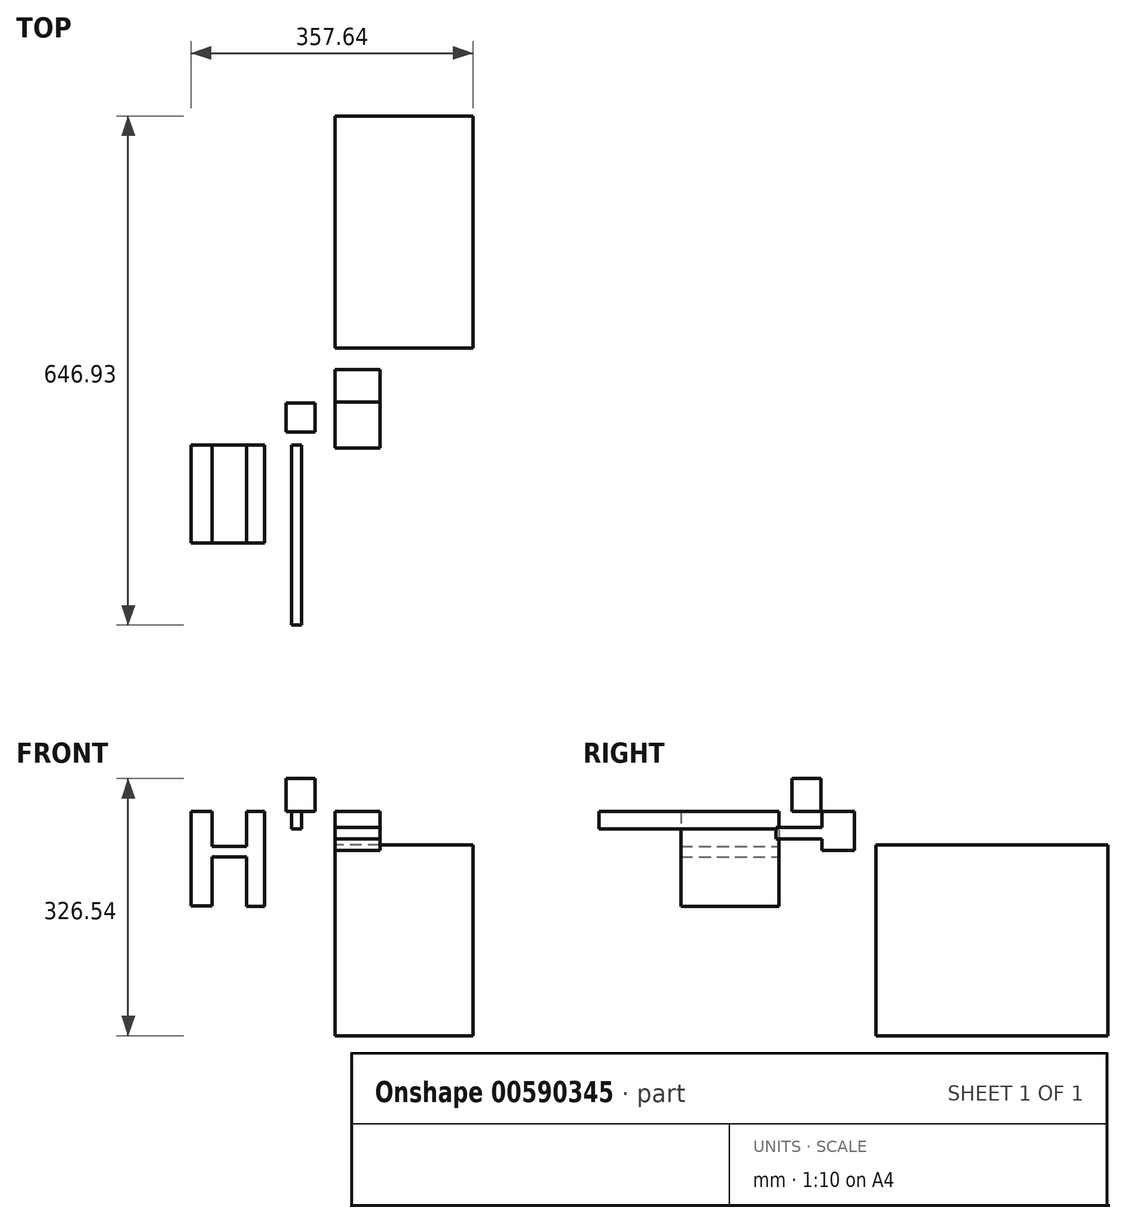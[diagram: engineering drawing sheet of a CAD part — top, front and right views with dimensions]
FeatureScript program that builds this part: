
annotation { "Feature Type Name" : "Feature", "Feature Type Description" : "" }
export const myFeature = defineFeature(function(context is Context, id is Id, definition is map)
    precondition{}
    {
        {
            var Q0;
            Q0=qCreatedBy(makeId("Top.planeOp"),FACE);
            var sketch = newSketch(context, id + "F0", { "sketchPlane" : qUnion([Q0])});
            skLineSegment(sketch, "E0.bottom", {"start": v(-61.98, 53.7) * mm, "end": v(-25.24, 53.7) * mm});
            skLineSegment(sketch, "E0.top", {"start": v(-61.98, 16.97) * mm, "end": v(-25.24, 16.97) * mm});
            skLineSegment(sketch, "E0.left", {"start": v(-61.98, 53.7) * mm, "end": v(-61.98, 16.97) * mm});
            skLineSegment(sketch, "E0.right", {"start": v(-25.24, 53.7) * mm, "end": v(-25.24, 16.97) * mm});
            skSolve(sketch);
        }
        {
            var Q0;
            Q0 = qSketchRegion(id + "F0", true);
            extrude(context, id + "F1", {"entities" : qUnion([Q0]), "depth" : 41.9 * mm, "offsetDistance" : 25.4 * mm});
        }
        {
            var Q0;
            Q0=qCreatedBy(makeId("Right.planeOp"),FACE);
            var sketch = newSketch(context, id + "F2", { "sketchPlane" : qUnion([Q0])});
            skLineSegment(sketch, "E1.bottom", {"start": v(-3.45, -2.4) * mm, "end": v(45.33, -2.4) * mm});
            skLineSegment(sketch, "E1.top", {"start": v(-3.45, -60.14) * mm, "end": v(45.33, -60.14) * mm});
            skLineSegment(sketch, "E1.left", {"start": v(-3.45, -2.4) * mm, "end": v(-3.45, -60.14) * mm});
            skLineSegment(sketch, "E1.right", {"start": v(45.33, -2.4) * mm, "end": v(45.33, -60.14) * mm});
            skSolve(sketch);
        }
        {
            var Q0;
            Q0=makeQuery(id+"F2.imprint","IMPRINT",FACE,{"disambiguationData":[TD([[makeQuery(id+"F2.imprint","IMPRINT",EDGE,{"derivedFrom":sQuery(id+"F2.wireOp",EDGE,"E1.bottom")}),-1.0]])]});
            var sketch = newSketch(context, id + "F3", { "sketchPlane" : qUnion([Q0])});
            skLineSegment(sketch, "E2.bottom", {"start": v(55.1, 0) * mm, "end": v(96.37, 0) * mm});
            skLineSegment(sketch, "E2.top", {"start": v(55.1, -49.58) * mm, "end": v(96.37, -49.58) * mm});
            skLineSegment(sketch, "E2.left", {"start": v(55.1, 0) * mm, "end": v(55.1, -49.58) * mm});
            skLineSegment(sketch, "E2.right", {"start": v(96.37, 0) * mm, "end": v(96.37, -49.58) * mm});
            skLineSegment(sketch, "E3.bottom", {"start": v(73.86, -20.04) * mm, "end": v(-71.23, -20.04) * mm});
            skLineSegment(sketch, "E3.top", {"start": v(73.86, -34.81) * mm, "end": v(-71.23, -34.81) * mm});
            skLineSegment(sketch, "E3.left", {"start": v(73.86, -20.04) * mm, "end": v(73.86, -34.81) * mm});
            skLineSegment(sketch, "E3.right", {"start": v(-71.23, -20.04) * mm, "end": v(-71.23, -34.81) * mm});
            skSolve(sketch);
        }
        {
            var Q0;
            {var subQ4=sQuery(id+"F3.wireOp",EDGE,"E2.bottom");Q0=makeQuery(id+"F3.imprint","IMPRINT",FACE,{"disambiguationData":[TD([[makeQuery(id+"F3.imprint","IMPRINT",EDGE,{"derivedFrom":subQ4}),-1.0]])]});}
            var Q1;
            {var subQ5=sQuery(id+"F3.wireOp",EDGE,"E3.left");Q1=makeQuery(id+"F3.imprint","IMPRINT",FACE,{"disambiguationData":[TD([[makeQuery(id+"F3.imprint","IMPRINT",EDGE,{"derivedFrom":subQ5}),-1.0]])]});}
            var Q2;
            {var subQ0=sQuery(id+"F3.wireOp",EDGE,"E3.bottom");var subQ1=sQuery(id+"F3.wireOp",EDGE,"E2.left");var subQ2=makeQuery(id+"F3.imprint","INTERSECT",VERTEX,{"derivedFrom":[subQ1,subQ0]});Q2=makeQuery(id+"F3.imprint","IMPRINT",FACE,{"disambiguationData":[TD([[makeQuery(id+"F3.imprint","IMPRINT",EDGE,{"disambiguationData":[TD([[subQ2,-1.0]])],"derivedFrom":subQ1}),-1.0]])]});}
            var Q3;
            {var subQ0=sQuery(id+"F3.wireOp",EDGE,"E3.bottom");var subQ1=makeQuery(id+"F2.imprint","IMPRINT",EDGE,{"derivedFrom":sQuery(id+"F2.wireOp",EDGE,"E1.right")});var subQ2=makeQuery(id+"F3.imprint","INTERSECT",VERTEX,{"derivedFrom":[subQ1,subQ0]});Q3=makeQuery(id+"F3.imprint","IMPRINT",FACE,{"disambiguationData":[TD([[makeQuery(id+"F3.imprint","IMPRINT",EDGE,{"disambiguationData":[TD([[subQ2,-1.0]])],"derivedFrom":subQ0}),1.0]])]});}
            extrude(context, id + "F4", {"entities" : qUnion([Q0, Q1, Q2, Q3]), "depth" : 57.15 * mm, "offsetDistance" : 25.4 * mm});
        }
        {
            var Q0;
            Q0=qCreatedBy(makeId("Right.planeOp"),FACE);
            var sketch = newSketch(context, id + "F5", { "sketchPlane" : qUnion([Q0])});
            skLineSegment(sketch, "E4.bottom", {"start": v(123.59, -42.1) * mm, "end": v(418.33, -42.1) * mm});
            skLineSegment(sketch, "E4.top", {"start": v(123.59, -284.63) * mm, "end": v(418.33, -284.63) * mm});
            skLineSegment(sketch, "E4.left", {"start": v(123.59, -42.1) * mm, "end": v(123.59, -284.63) * mm});
            skLineSegment(sketch, "E4.right", {"start": v(418.33, -42.1) * mm, "end": v(418.33, -284.63) * mm});
            skSolve(sketch);
        }
        {
            var Q0;
            Q0=makeQuery(id+"F5.imprint","IMPRINT",FACE,{"disambiguationData":[TD([[makeQuery(id+"F5.imprint","IMPRINT",EDGE,{"derivedFrom":sQuery(id+"F5.wireOp",EDGE,"E4.bottom")}),-1.0]])]});
            extrude(context, id + "F6", {"entities" : qUnion([Q0]), "depth" : 175.26 * mm, "offsetDistance" : 25.4 * mm});
        }
        {
            var Q0;
            Q0=qCreatedBy(makeId("Front.planeOp"),FACE);
            var sketch = newSketch(context, id + "F7", { "sketchPlane" : qUnion([Q0])});
            skLineSegment(sketch, "E5.bottom", {"start": v(-156.26, 0) * mm, "end": v(-182.38, 0) * mm});
            skLineSegment(sketch, "E5.top", {"start": v(-156.26, -120.05) * mm, "end": v(-182.38, -120.05) * mm});
            skLineSegment(sketch, "E5.left", {"start": v(-156.26, 0) * mm, "end": v(-156.26, -120.05) * mm});
            skLineSegment(sketch, "E5.right", {"start": v(-182.38, 0) * mm, "end": v(-182.38, -120.05) * mm});
            skLineSegment(sketch, "E6.bottom", {"start": v(-163.44, -44.3) * mm, "end": v(-96.83, -44.3) * mm});
            skLineSegment(sketch, "E6.top", {"start": v(-163.44, -57.36) * mm, "end": v(-96.83, -57.36) * mm});
            skLineSegment(sketch, "E6.left", {"start": v(-163.44, -44.3) * mm, "end": v(-163.44, -57.36) * mm});
            skLineSegment(sketch, "E6.right", {"start": v(-96.83, -44.3) * mm, "end": v(-96.83, -57.36) * mm});
            skLineSegment(sketch, "E7.bottom", {"start": v(-112.5, 0) * mm, "end": v(-89.64, 0) * mm});
            skLineSegment(sketch, "E7.top", {"start": v(-112.5, -120.7) * mm, "end": v(-89.64, -120.7) * mm});
            skLineSegment(sketch, "E7.left", {"start": v(-112.5, 0) * mm, "end": v(-112.5, -120.7) * mm});
            skLineSegment(sketch, "E7.right", {"start": v(-89.64, 0) * mm, "end": v(-89.64, -120.7) * mm});
            skSolve(sketch);
        }
        {
            var Q0;
            Q0 = qSketchRegion(id + "F7", true);
            var Q1;
            {var subQ4=sQuery(id+"F7.wireOp",EDGE,"E5.bottom");Q1=makeQuery(id+"F7.imprint","IMPRINT",FACE,{"disambiguationData":[TD([[makeQuery(id+"F7.imprint","IMPRINT",EDGE,{"derivedFrom":subQ4}),1.0]])]});}
            extrude(context, id + "F8", {"entities" : qUnion([Q0, Q1]), "depth" : 124.46 * mm, "offsetDistance" : 25.4 * mm});
        }
        {
            var Q0;
            Q0=qCreatedBy(makeId("Front.planeOp"),FACE);
            var sketch = newSketch(context, id + "F9", { "sketchPlane" : qUnion([Q0])});
            skLineSegment(sketch, "E8.bottom", {"start": v(-54.83, -48.87) * mm, "end": v(-42.42, -48.87) * mm});
            skLineSegment(sketch, "E8.top", {"start": v(-54.83, -101.77) * mm, "end": v(-42.42, -101.77) * mm});
            skLineSegment(sketch, "E8.left", {"start": v(-54.83, -48.87) * mm, "end": v(-54.83, -101.77) * mm});
            skLineSegment(sketch, "E8.right", {"start": v(-42.42, -48.87) * mm, "end": v(-42.42, -101.77) * mm});
            skLineSegment(sketch, "E9.bottom", {"start": v(-42.42, -101.77) * mm, "end": v(-54.83, -101.77) * mm});
            skLineSegment(sketch, "E9.top", {"start": v(-42.42, -122.66) * mm, "end": v(-54.83, -122.66) * mm});
            skLineSegment(sketch, "E9.left", {"start": v(-42.42, -101.77) * mm, "end": v(-42.42, -122.66) * mm});
            skLineSegment(sketch, "E9.right", {"start": v(-54.83, -101.77) * mm, "end": v(-54.83, -122.66) * mm});
            skLineSegment(sketch, "E10.bottom", {"start": v(-54.83, 0) * mm, "end": v(-42.42, 0) * mm});
            skLineSegment(sketch, "E10.top", {"start": v(-54.83, -22.1) * mm, "end": v(-42.42, -22.1) * mm});
            skLineSegment(sketch, "E10.left", {"start": v(-54.83, 0) * mm, "end": v(-54.83, -22.1) * mm});
            skLineSegment(sketch, "E10.right", {"start": v(-42.42, 0) * mm, "end": v(-42.42, -22.1) * mm});
            skSolve(sketch);
        }
        {
            var Q0;
            Q0=makeQuery(id+"F9.imprint","IMPRINT",FACE,{"disambiguationData":[TD([[makeQuery(id+"F9.imprint","IMPRINT",EDGE,{"derivedFrom":sQuery(id+"F9.wireOp",EDGE,"E10.bottom")}),-1.0]])]});
            var Q1;
            Q1=makeQuery(id+"F9.imprint","IMPRINT",FACE,{"disambiguationData":[TD([[makeQuery(id+"F9.imprint","IMPRINT",EDGE,{"derivedFrom":sQuery(id+"F9.wireOp",EDGE,"E9.bottom")}),1.0]])]});
            extrude(context, id + "F10", {"entities" : qUnion([Q0, Q1]), "depth" : 228.6 * mm, "offsetDistance" : 25.4 * mm});
        }
    });
